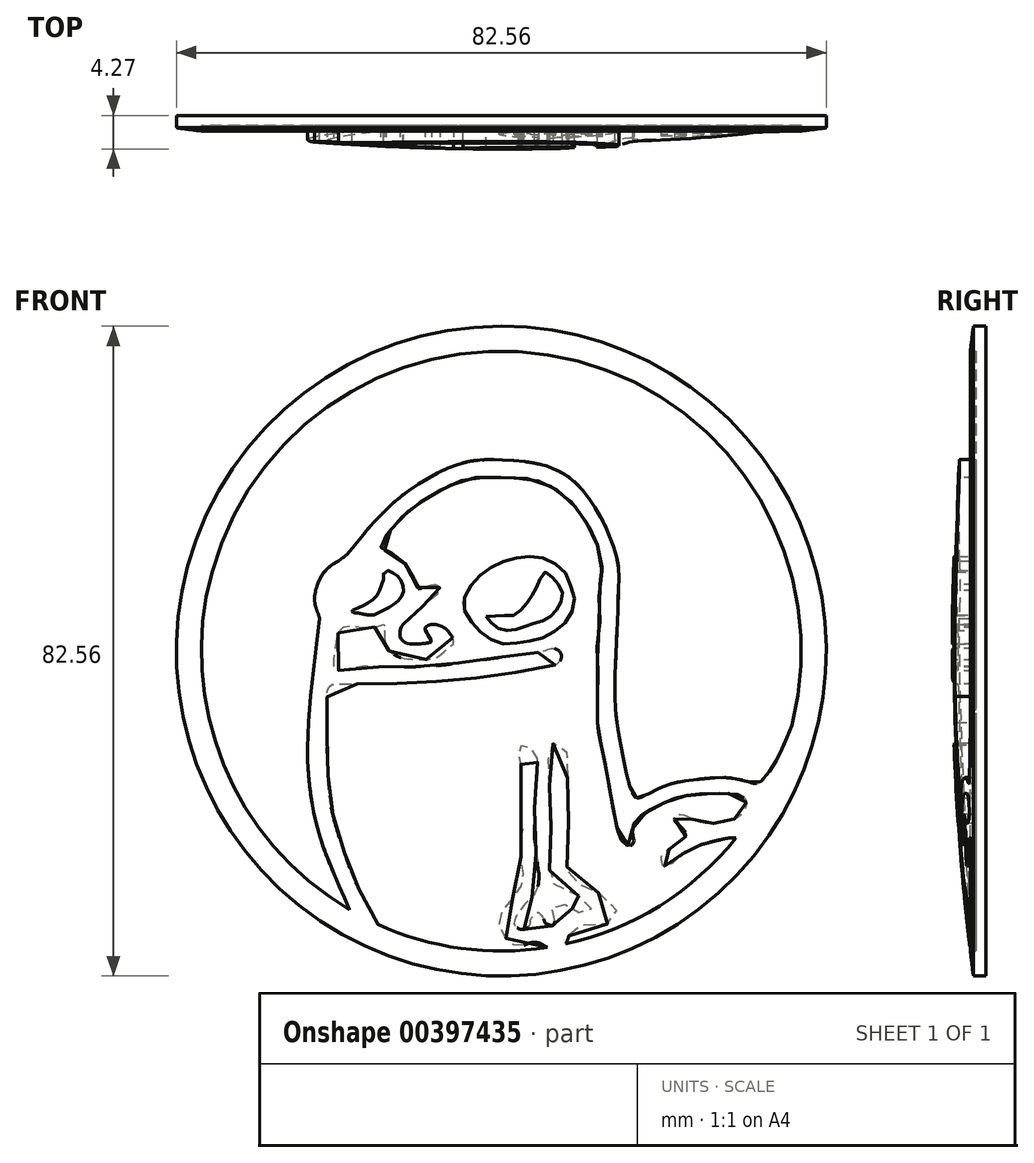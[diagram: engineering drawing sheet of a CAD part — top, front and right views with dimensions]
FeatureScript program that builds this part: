
annotation { "Feature Type Name" : "Feature", "Feature Type Description" : "" }
export const myFeature = defineFeature(function(context is Context, id is Id, definition is map)
    precondition{}
    {
        {
            var Q0;
            Q0=qCreatedBy(makeId("Front.planeOp"),FACE);
            var sketch = newSketch(context, id + "F0", { "sketchPlane" : qUnion([Q0])});
            skCircle(sketch, "E0", {"center": v(0, 0) * mm, "radius": 41.28 * mm});
            skArc(sketch, "E1", {"start": v(-15.7, -34.72) * mm, "mid": v(-5.14, -37.75) * mm, "end": v(5.84, -37.65) * mm});
            skFitSpline(sketch, "E2", {"points": [v(-19.29, -32.86) * mm, v(-20.97, -28.94) * mm, v(-22.72, -24.57) * mm, v(-24.26, -17.86) * mm, v(-24.5, -9.16) * mm, v(-23.07, 4.17) * mm], "startDerivative": vector(-10.89, 25.44) * mm, "endDerivative": vector(6.46, 50.7) * mm});
            skFitSpline(sketch, "E3", {"points": [v(-23.07, 4.17) * mm, v(-23.7, 6.25) * mm, v(-23.4, 8.35) * mm, v(-22.43, 10.12) * mm, v(-20.66, 11.43) * mm], "startDerivative": vector(-3.05, 9.11) * mm, "endDerivative": vector(8.76, 3.77) * mm});
            skFitSpline(sketch, "E4", {"points": [v(-20.66, 11.43) * mm, v(-20.14, 11.8) * mm, v(-18.59, 13.44) * mm, v(-16.68, 15.84) * mm, v(-13.22, 19.25) * mm, v(-9.29, 21.98) * mm, v(-4.83, 23.93) * mm, v(-0.8, 24.33) * mm, v(3.79, 23.95) * mm, v(7.1, 22.96) * mm], "startDerivative": vector(9.62, 5.7) * mm, "endDerivative": vector(22.89, -12.21) * mm});
            skFitSpline(sketch, "E5", {"points": [v(7.1, 22.96) * mm, v(8.35, 22.25) * mm, v(9.8, 21.03) * mm, v(11.63, 18.66) * mm, v(13.13, 16.07) * mm, v(14.34, 13.03) * mm, v(14.87, 10.67) * mm, v(14.8, 5.29) * mm, v(14.52, -1.36) * mm, v(14.42, -5.76) * mm], "startDerivative": vector(17.16, -8.92) * mm, "endDerivative": vector(0.8, -34.81) * mm});
            skFitSpline(sketch, "E6", {"points": [v(14.42, -5.76) * mm, v(14.56, -8.05) * mm, v(15.2, -12.12) * mm, v(15.93, -15.67) * mm, v(16.36, -17.36) * mm, v(16.72, -18.19) * mm, v(17.14, -18.62) * mm, v(17.84, -18.53) * mm, v(19.47, -17.72) * mm, v(21.82, -16.79) * mm, v(24.29, -16.37) * mm, v(27.88, -16.06) * mm, v(29.83, -16.23) * mm, v(31.42, -16.6) * mm, v(31.85, -16.75) * mm, v(32.52, -16.79) * mm, v(33.21, -16.3) * mm, v(34.86, -14) * mm, v(36.92, -9.42) * mm], "startDerivative": vector(1.24, -34.63) * mm, "endDerivative": vector(21.35, 54.06) * mm});
            skFitSpline(sketch, "E7", {"points": [v(-15.7, -34.72) * mm, v(-16.36, -33.38) * mm, v(-17.1, -32) * mm, v(-18.4, -29.6) * mm, v(-19.13, -27.9) * mm, v(-20.19, -24.87) * mm, v(-21.09, -21.97) * mm, v(-21.9, -18.06) * mm, v(-22.09, -13.52) * mm, v(-22.15, -11.53) * mm, v(-22.1, -5.39) * mm, v(-22.08, -4.88) * mm, v(-21.93, -4.57) * mm, v(-21.69, -4.36) * mm, v(-21.34, -4.2) * mm, v(-20.64, -4.16) * mm, v(-14.4, -4.12) * mm, v(-11.54, -4) * mm, v(-5.4, -3.62) * mm, v(0.5, -2.88) * mm, v(6.25, -1.94) * mm, v(6.93, -1.72) * mm, v(7.31, -1.45) * mm, v(7.57, -1.05) * mm, v(7.6, -0.42) * mm, v(7.38, 0) * mm, v(6.75, 0.31) * mm, v(5.37, 0) * mm, v(3.27, -0.36) * mm, v(0.46, -0.72) * mm, v(-1.92, -1.04) * mm, v(-5.34, -1.52) * mm, v(-8.43, -1.87) * mm, v(-11.07, -1.98) * mm, v(-15, -2.01) * mm, v(-17.83, -1.97) * mm, v(-19.06, -2.19) * mm, v(-20.2, -2.45) * mm, v(-20.82, -2.43) * mm, v(-21.28, -1.93) * mm, v(-21.22, -0.82) * mm, v(-20.92, 1.33) * mm, v(-20.7, 2.41) * mm, v(-20.22, 2.94) * mm, v(-19.75, 3.2) * mm, v(-18.44, 3.09) * mm, v(-16.66, 3.02) * mm, v(-15.56, 3.17) * mm, v(-14.96, 3.37) * mm, v(-14.73, 3.37) * mm, v(-14.63, 3.27) * mm, v(-14.78, 3) * mm, v(-14.86, 1.9) * mm, v(-14.8, 1.2) * mm, v(-14.54, 0.45) * mm, v(-14.23, 0) * mm, v(-13.59, -0.46) * mm, v(-12.74, -0.83) * mm, v(-11.42, -1.03) * mm, v(-9.96, -1.1) * mm, v(-8.92, -1.02) * mm, v(-8.03, -0.68) * mm, v(-7.17, 0) * mm, v(-6.18, 0.84) * mm, v(-6.08, 0.9) * mm, v(-6.08, 1.42) * mm, v(-6.46, 2.14) * mm, v(-6.98, 2.78) * mm, v(-7.85, 3.25) * mm, v(-8.5, 3.4) * mm, v(-9.24, 3.28) * mm, v(-9.67, 2.92) * mm, v(-9.5, 2.43) * mm, v(-9.09, 1.67) * mm, v(-8.95, 1.41) * mm, v(-8.88, 1.2) * mm, v(-9.47, 1.02) * mm, v(-10.77, 0.9) * mm, v(-11.73, 0.95) * mm, v(-12.43, 1.22) * mm, v(-12.8, 1.68) * mm, v(-12.82, 2.76) * mm, v(-12.48, 3.4) * mm], "startDerivative": vector(-53.04, 103.01) * mm, "endDerivative": vector(38.6, 61.83) * mm});
            skFitSpline(sketch, "E8", {"points": [v(-12.48, 3.4) * mm, v(-12.06, 3.86) * mm, v(-11.08, 4.77) * mm, v(-9.89, 5.8) * mm, v(-8.58, 6.92) * mm, v(-8.08, 7.33) * mm, v(-8.02, 7.47) * mm, v(-8, 7.63) * mm, v(-7.86, 7.87) * mm, v(-7.8, 8.06) * mm, v(-8.07, 8.33) * mm, v(-8.41, 8.44) * mm, v(-9.25, 8.25) * mm, v(-10.3, 7.74) * mm, v(-10.48, 7.75) * mm, v(-10.68, 8.13) * mm, v(-11.1, 9.18) * mm, v(-11.67, 10.27) * mm, v(-12.33, 11.2) * mm, v(-13.12, 11.97) * mm, v(-14.03, 12.53) * mm, v(-14.8, 12.77) * mm, v(-15.05, 12.93) * mm, v(-15.28, 13.14) * mm, v(-15.32, 13.67) * mm, v(-15.02, 14.23) * mm, v(-13.84, 15.7) * mm, v(-12.48, 17.15) * mm, v(-11, 18.4) * mm, v(-9.4, 19.5) * mm, v(-7.35, 20.67) * mm, v(-5.48, 21.5) * mm, v(-4.3, 21.9) * mm, v(-2.27, 22.08) * mm, v(1.65, 21.99) * mm, v(3.9, 21.82) * mm, v(5.34, 21.37) * mm, v(6.57, 20.78) * mm, v(8.49, 19.35) * mm, v(9.92, 17.72) * mm, v(11.18, 15.77) * mm, v(11.8, 14.58) * mm, v(12.27, 13.16) * mm, v(12.7, 11.13) * mm, v(12.8, 10.07) * mm, v(12.63, 8.85) * mm, v(12.43, 7.65) * mm, v(12.48, 5.69) * mm, v(12.4, 2) * mm, v(12.1, 0) * mm, v(12.27, -1.57) * mm, v(12.16, -6.55) * mm, v(12.23, -9.22) * mm], "startDerivative": vector(27.13, 32) * mm, "endDerivative": vector(6.26, -75.07) * mm});
            skFitSpline(sketch, "E9", {"points": [v(12.22, -9.1) * mm, v(12.35, -10.16) * mm, v(12.72, -12.13) * mm, v(13.25, -14.7) * mm, v(13.84, -18.02) * mm, v(14.38, -20.86) * mm, v(14.78, -22.73) * mm, v(15.16, -23.84) * mm, v(15.59, -24.43) * mm, v(15.96, -24.66) * mm, v(16.36, -24.76) * mm, v(16.67, -24.63) * mm, v(16.87, -24.37) * mm, v(16.78, -23.78) * mm, v(16.65, -22.83) * mm, v(16.83, -21.92) * mm, v(17.93, -20.8) * mm, v(19.4, -19.91) * mm, v(21.18, -19.01) * mm, v(23.33, -18.38) * mm, v(25.27, -18.16) * mm, v(29.85, -18.2) * mm, v(30.64, -18.51) * mm, v(31.03, -18.9) * mm, v(31.1, -19.46) * mm, v(30.8, -20.32) * mm, v(30.29, -20.95) * mm, v(29.43, -21.41) * mm, v(28.14, -21.78) * mm, v(27.13, -21.9) * mm, v(25.86, -21.88) * mm, v(24.8, -21.58) * mm, v(23.86, -21.1) * mm, v(23.15, -20.84) * mm, v(22.35, -20.8) * mm, v(22.07, -21) * mm, v(21.99, -21.2) * mm, v(22.03, -21.5) * mm, v(22.4, -21.96) * mm, v(22.83, -22.36) * mm, v(23.24, -22.77) * mm, v(23.42, -23.01) * mm, v(23.44, -23.55) * mm, v(22.75, -24.13) * mm, v(21.87, -24.7) * mm, v(20.83, -25.52) * mm, v(20.36, -26) * mm, v(20.29, -26.53) * mm, v(20.44, -27.12) * mm, v(20.78, -27.29) * mm, v(21.26, -27.2) * mm, v(21.84, -26.82) * mm, v(22.5, -26.2) * mm, v(23.46, -25.47) * mm, v(24.7, -24.82) * mm, v(26.27, -24.34) * mm, v(28.08, -23.9) * mm, v(29.46, -23.7) * mm, v(29.82, -23.72) * mm], "startDerivative": vector(6.25, -55.49) * mm, "endDerivative": vector(27.91, -1.77) * mm});
            skFitSpline(sketch, "E10", {"points": [v(28.08, -23.9) * mm, v(29.34, -23.63) * mm, v(29.86, -23.66) * mm], "startDerivative": vector(2.27, 0.58) * mm, "endDerivative": vector(1.15, -0.12) * mm});
            skFitSpline(sketch, "E11", {"points": [v(5.84, -37.65) * mm, v(5.32, -37.33) * mm, v(4.82, -37.07) * mm, v(3.98, -37.02) * mm, v(3.59, -37.09) * mm, v(2.84, -37.36) * mm, v(2.12, -37.45) * mm, v(1.47, -37.3) * mm, v(0.8, -36.75) * mm, v(0.14, -35.7) * mm, v(-0.22, -34.9) * mm, v(-0.2, -33.8) * mm, v(0.46, -32.65) * mm, v(1.74, -31) * mm, v(2.53, -29.83) * mm, v(2.81, -29.1) * mm, v(2.8, -27.79) * mm, v(2.47, -26.09) * mm, v(2.39, -24.42) * mm, v(2.64, -22.95) * mm, v(2.74, -22.53) * mm, v(2.63, -21.67) * mm, v(2.5, -21.11) * mm, v(2.5, -20.41) * mm, v(2.57, -19.28) * mm, v(2.6, -17.71) * mm, v(2.44, -16.5) * mm, v(2.46, -14.93) * mm, v(2.5, -14.2) * mm, v(2.38, -13.25) * mm, v(2.19, -12.77) * mm, v(2.36, -12.26) * mm, v(2.62, -11.95) * mm, v(3.12, -11.93) * mm, v(3.8, -12.4) * mm, v(4.42, -13.28) * mm, v(4.6, -14.26) * mm, v(4.6, -15.9) * mm, v(4.48, -16.8) * mm, v(4.43, -18.2) * mm, v(4.3, -18.66) * mm, v(4.2, -22.9) * mm, v(4.27, -24.2) * mm, v(4.37, -24.7) * mm, v(4.4, -25.64) * mm, v(4.54, -26.25) * mm, v(4.6, -27.07) * mm, v(4.67, -27.76) * mm, v(4.78, -28.32) * mm, v(4.73, -29.36) * mm, v(4.6, -30) * mm, v(4.3, -30.69) * mm, v(3.84, -31.34) * mm, v(3.6, -31.59) * mm, v(3.24, -31.9) * mm, v(2.78, -32.37) * mm, v(2.3, -33.05) * mm, v(1.95, -33.57) * mm, v(1.73, -34.07) * mm, v(1.63, -34.49) * mm, v(1.73, -34.88) * mm, v(2.05, -35.18) * mm, v(2.38, -35.34) * mm, v(2.97, -35.34) * mm, v(3.35, -35.12) * mm, v(3.67, -34.7) * mm, v(3.7, -34.23) * mm, v(3.9, -33.8) * mm, v(4.23, -33.44) * mm, v(4.63, -33.18) * mm, v(5.08, -33.55) * mm, v(5.4, -34.1) * mm, v(5.5, -34.4) * mm, v(5.78, -34.64) * mm, v(6.27, -34.85) * mm, v(6.6, -34.86) * mm, v(6.75, -34.49) * mm, v(6.86, -34.2) * mm, v(6.93, -33.9) * mm, v(6.73, -33.42) * mm, v(6.48, -32.74) * mm, v(6.48, -32.5) * mm, v(6.85, -32.16) * mm, v(7.3, -31.99) * mm, v(7.9, -32.09) * mm, v(8.63, -32.48) * mm, v(9.17, -32.77) * mm, v(9.5, -33) * mm, v(9.85, -33.18) * mm, v(10.3, -33.28) * mm, v(10.78, -33.24) * mm, v(11.2, -32.96) * mm, v(11.46, -32.74) * mm, v(11.51, -32.37) * mm, v(11.33, -31.99) * mm, v(10.14, -31.27) * mm, v(8.2, -30.42) * mm, v(6.99, -29.82) * mm, v(6.4, -29.23) * mm, v(6.22, -28.7) * mm, v(6.15, -27.89) * mm, v(6.28, -22.96) * mm, v(6.5, -21.03) * mm, v(6.6, -20.36) * mm, v(6.45, -19.87) * mm, v(6.2, -19.24) * mm, v(6.08, -18.93) * mm, v(6.09, -17.59) * mm, v(6.14, -17.14) * mm, v(6.15, -15.19) * mm, v(6.06, -14.2) * mm, v(5.88, -12.95) * mm, v(6, -12.27) * mm, v(6.47, -11.8) * mm, v(6.9, -11.66) * mm, v(7.35, -11.7) * mm, v(7.93, -12.2) * mm, v(8.33, -12.86) * mm, v(8.4, -13.89) * mm, v(8.47, -17.74) * mm, v(8.52, -20.4) * mm, v(8.56, -22.42) * mm, v(8.48, -25.37) * mm, v(8.39, -25.79) * mm, v(8.39, -26.92) * mm, v(8.3, -27.5) * mm, v(8.45, -28.15) * mm, v(8.87, -28.86) * mm, v(9.45, -29.4) * mm, v(10.4, -29.73) * mm, v(11.27, -30.14) * mm, v(12.5, -30.8) * mm, v(13.52, -31.7) * mm, v(14.4, -32.6) * mm, v(14.72, -33.21) * mm, v(14.37, -34.15) * mm, v(13.72, -34.6) * mm, v(12.69, -34.8) * mm, v(11.19, -34.84) * mm, v(9.8, -34.88) * mm, v(9.24, -35.08) * mm, v(8.87, -35.39) * mm, v(8.59, -36.14) * mm, v(8.13, -37.22) * mm], "startDerivative": vector(-91.64, 48.63) * mm, "endDerivative": vector(-71.66, -81.6) * mm});
            skFitSpline(sketch, "E12", {"points": [v(8.04, -37.24) * mm, v(8.29, -36.86) * mm, v(8.59, -36.14) * mm], "startDerivative": vector(0.63, 0.7) * mm, "endDerivative": vector(0.5, 1.38) * mm});
            skFitSpline(sketch, "E13", {"points": [v(-18.86, 5.24) * mm, v(-17.96, 5.57) * mm, v(-17.12, 6.01) * mm, v(-16.23, 6.62) * mm, v(-15.54, 7.52) * mm, v(-15.16, 8.52) * mm, v(-14.97, 9.3) * mm, v(-14.95, 9.86) * mm, v(-14.6, 10.16) * mm, v(-14.36, 10.22) * mm, v(-13.72, 9.92) * mm, v(-13.26, 9.6) * mm, v(-12.76, 9.05) * mm, v(-12.51, 8.5) * mm, v(-12.41, 7.85) * mm, v(-12.57, 7.11) * mm, v(-13.08, 6.39) * mm, v(-13.95, 5.73) * mm, v(-15.09, 5.15) * mm, v(-15.84, 4.78) * mm, v(-16.17, 4.62) * mm, v(-17.2, 4.63) * mm, v(-18.22, 4.83) * mm, v(-18.92, 4.98) * mm, v(-18.86, 5.24) * mm]});
            skFitSpline(sketch, "E14", {"points": [v(-4.66, 5.14) * mm, v(-4.85, 5.6) * mm, v(-4.78, 6.54) * mm, v(-4.2, 7.87) * mm, v(-3.17, 9.13) * mm, v(-1.7, 10.36) * mm, v(-0.36, 11.12) * mm, v(0.83, 11.57) * mm, v(2.77, 11.93) * mm, v(4.62, 11.98) * mm, v(6.15, 11.47) * mm, v(7.41, 10.64) * mm, v(8.22, 9.77) * mm, v(8.57, 9.13) * mm, v(8.95, 8) * mm, v(9.2, 7.53) * mm, v(9.23, 5.77) * mm, v(8.76, 4.63) * mm, v(7.93, 3.42) * mm, v(6.45, 2.28) * mm, v(5.13, 1.64) * mm, v(3.35, 1.22) * mm, v(0, 0.97) * mm, v(-1.3, 1.47) * mm, v(-2.3, 2.16) * mm, v(-3.6, 3.42) * mm, v(-4.66, 5.14) * mm]});
            skFitSpline(sketch, "E15", {"points": [v(-1.92, 4.42) * mm, v(0.39, 4.52) * mm, v(1.37, 4.55) * mm, v(1.83, 4.6) * mm, v(2.33, 5.03) * mm, v(3.36, 6.24) * mm, v(4.14, 7.43) * mm, v(4.76, 8.68) * mm, v(5.16, 9.68) * mm, v(5.39, 9.95) * mm, v(5.56, 10.04) * mm, v(5.78, 9.99) * mm, v(6.3, 9.55) * mm, v(6.87, 8.97) * mm, v(7.38, 8.23) * mm, v(7.69, 7.55) * mm, v(7.77, 6.87) * mm, v(7.38, 5.89) * mm, v(6.48, 4.6) * mm, v(5.51, 3.94) * mm, v(4.61, 3.66) * mm, v(3.85, 3.42) * mm, v(2.78, 3.03) * mm, v(1.75, 2.72) * mm, v(0.84, 2.61) * mm, v(0.08, 2.68) * mm, v(-0.58, 3) * mm, v(-1.77, 4.13) * mm, v(-1.92, 4.3) * mm, v(-1.98, 4.39) * mm, v(-1.92, 4.42) * mm]});
            skArc(sketch, "E16.trimOffspring", {"start": v(8.04, -37.24) * mm, "mid": v(20.13, -32.35) * mm, "end": v(29.86, -23.66) * mm});
            skArc(sketch, "E17.trimOffspring", {"start": v(36.92, -9.42) * mm, "mid": v(-14.66, 35.16) * mm, "end": v(-19.29, -32.86) * mm});
            skLineSegment(sketch, "E18", {"start": v(-20.67, 11.43) * mm, "end": v(-20.66, 11.43) * mm});
            skLineSegment(sketch, "E19", {"start": v(7.1, 22.96) * mm, "end": v(7.1, 22.96) * mm});
            skSolve(sketch);
        }
        {
            var Q0;
            Q0=qCreatedBy(makeId("Front.planeOp"),FACE);
            var sketch = newSketch(context, id + "F1", { "sketchPlane" : qUnion([Q0])});
            skCircle(sketch, "E20", {"center": v(0, 0) * mm, "radius": 41.28 * mm});
            skSolve(sketch);
        }
        {
            var Q0;
            Q0 = qSketchRegion(id + "F1", true);
            extrude(context, id + "F2", {"entities" : qUnion([Q0]), "depth" : 5.08 * mm, "hasSecondDirection" : true, "secondDirectionOppositeDirection" : true, "secondDirectionDepth" : 1.27 * mm});
        }
        {
            var Q0;
            Q0=makeQuery(id+"F0.imprint","IMPRINT",FACE,{"disambiguationData":[TD([[makeQuery(id+"F0.imprint","IMPRINT",EDGE,{"derivedFrom":sQuery(id+"F0.wireOp",EDGE,"E1")}),1.0]])]});
            var Q1;
            Q1=makeQuery(id+"F0.imprint","IMPRINT",FACE,{"disambiguationData":[TD([[makeQuery(id+"F0.imprint","IMPRINT",EDGE,{"derivedFrom":sQuery(id+"F0.wireOp",EDGE,"E15")}),-1.0]])]});
            var Q2;
            Q2=makeQuery(id+"F0.imprint","IMPRINT",FACE,{"disambiguationData":[TD([[makeQuery(id+"F0.imprint","IMPRINT",EDGE,{"derivedFrom":sQuery(id+"F0.wireOp",EDGE,"E13")}),-1.0]])]});
            extrude(context, id + "F3", {"entities" : qUnion([Q0, Q1, Q2]), "operationType" : NewBodyOperationType.REMOVE, "depth" : 12.2 * mm});
        }
        {
            var Q0;
            Q0=makeQuery(id+"F0.imprint","IMPRINT",FACE,{"disambiguationData":[TD([[makeQuery(id+"F0.imprint","IMPRINT",EDGE,{"derivedFrom":sQuery(id+"F0.wireOp",EDGE,"E2")}),1.0]])]});
            extrude(context, id + "F4", {"entities" : qUnion([Q0]), "operationType" : NewBodyOperationType.REMOVE, "depth" : 25.32 * mm});
        }
        {
            var Q0;
            Q0=qCreatedBy(makeId("Top.planeOp"),FACE);
            var sketch = newSketch(context, id + "F5", { "sketchPlane" : qUnion([Q0])});
            skArc(sketch, "E21", {"start": v(-43.54, 0) * mm, "mid": v(-21.82, -2.25) * mm, "end": v(0, -3) * mm});
            skLineSegment(sketch, "E22", {"start": v(-64.55, 0) * mm, "end": v(-62.8, -31.58) * mm});
            skLineSegment(sketch, "E23", {"start": v(-62.8, -31.58) * mm, "end": v(0, -29.86) * mm});
            skLineSegment(sketch, "E24.trimOffspring", {"start": v(-43.54, 0) * mm, "end": v(-64.55, 0) * mm});
            skLineSegment(sketch, "E25", {"start": v(0, -3) * mm, "end": v(0, -18.69) * mm});
            skPoint(sketch, "E25.endSnap0", {"position": v(0, -3) * mm});
            skLineSegment(sketch, "E26", {"start": v(0, -18.69) * mm, "end": v(0, -29.86) * mm});
            skSolve(sketch);
        }
        {
            var Q0;
            Q0=makeQuery(id+"F5.imprint","IMPRINT",FACE,{"disambiguationData":[TD([[makeQuery(id+"F5.imprint","IMPRINT",EDGE,{"derivedFrom":sQuery(id+"F5.wireOp",EDGE,"E21")}),-1.0]])]});
            var Q1;
            Q1=sQuery(id+"F5.wireOp",EDGE,"E25");
            revolve(context, id + "F6", {"operationType" : NewBodyOperationType.REMOVE, "entities" : qUnion([Q0]), "axis" : qUnion([Q1]), "revolveType" : RevolveType.FULL, "oppositeDirection" : true});
        }
    });
